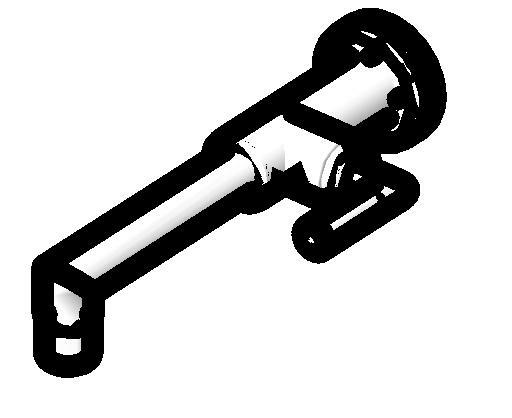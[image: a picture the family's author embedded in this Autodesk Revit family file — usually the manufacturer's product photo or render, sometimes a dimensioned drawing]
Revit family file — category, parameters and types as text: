
# Revit family: Deca_Torneira de parede para lavatório_Izy Plus_1178.24
name_source: partatom
category: Plumbing Fixtures
units: mm (PartAtom-declared; Revit-internal decimal feet)

## family parameters
Cut with Voids When Loaded = No
Host = Face
Part Type = Normal
Room Calculation Point = No
Round Connector Dimension = Use Radius
Shared = No

## types (1)
- 1178.C24_Cromado
    Acompanha o Produto = Acompanha Deca confort
    Aprovado por = quattroD
    Atendimento ao Cliente = 0800-0117073
    CWFU = 0
    Categoria = METAIS PARA BANHEIRO
    Composição Anel Vedação = -
    Composição Assento = -
    Composição Básica = Liga de Cobre (bronze e latão),Plásticos de Engenharia,Elastômeros
    Composição Componente = -
    Consumo = -
    Cor Interna = -
    Cor Principal = Cromado
    Cor Secundária = -
    Cores Componente = -
    Criado por = quattroD
    Código Pai = 1178.24
    Default Elevation = 1100 mm
    Description = Torneira de parede para lavatório
    Diâmetro Água Fria = 15 mm  [stored 0.0492126 ft]
    Informações Complementares = -
    Itens de Instalação = -
    Linha = Izy Plus
    Manufacturer = Deca
    Model = 1178.C24
    Norma = NBR10281
    Peso Líquido (Kg) = 1.023
    Pressão máx. funcionamento = 40 MCA
    Pressão mín. Aquec. Acúmulo = -
    Pressão mín. Aquec. Passagem = -
    Pressão mín. funcionamento = 2 MCA
    Raio Água Fria = 8 mm  [stored 0.0262467 ft]
    Saída de Esgoto = -
    Segmento = Banheiro Médio
    Tipo de dispositivo economizador = Sim
    Tipo de mecanismo utilizado = MVC -1/4 volta
    Tipo de rosca de entrada = BSP NBR 8133
    Tipo de rosca de saída = -
    Torneira = Deca_Cromado
    URL = www.deca.com.br
    Vazão na Pressão máx. (L/min) = 6
    Vazão na Pressão mín. (L/min) = 4

note: source unit labels omitted for Vazão na Pressão máx. (L/min), Vazão na Pressão mín. (L/min) — the stored unit's dimension contradicts the parameter name (converter mislabeling)

note: [stored X ft] marks values corroborated as IEEE doubles in the binary element streams (Revit-internal decimal feet)

## geometry (parser evidence)
native form markers: Sweep x3
no freeform markers — native parametric forms only
